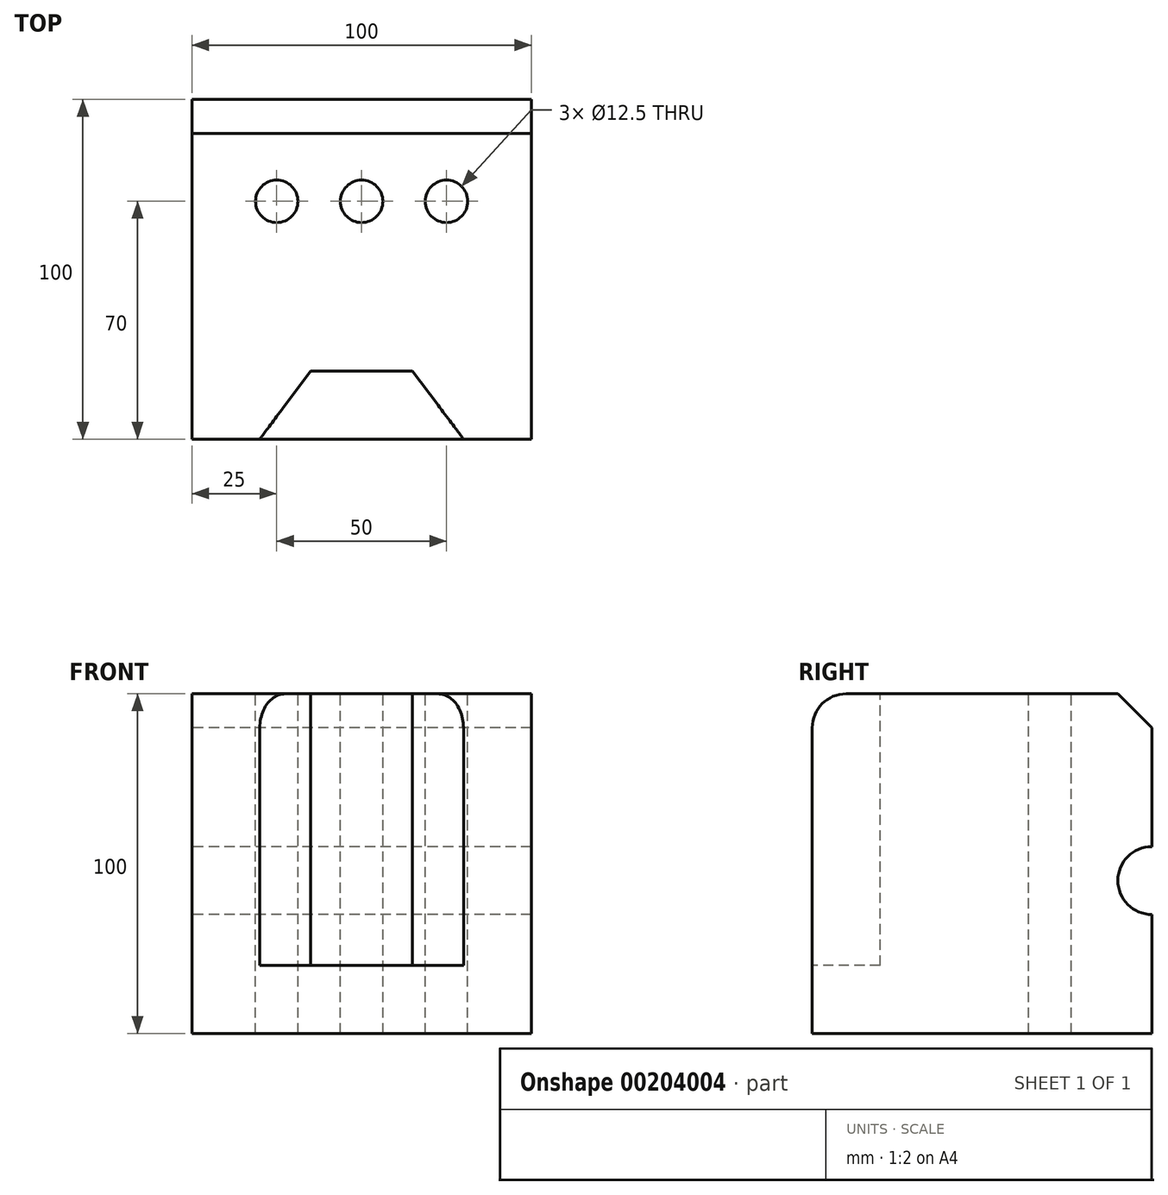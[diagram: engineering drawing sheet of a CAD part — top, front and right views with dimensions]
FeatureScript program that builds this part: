
annotation { "Feature Type Name" : "Feature", "Feature Type Description" : "" }
export const myFeature = defineFeature(function(context is Context, id is Id, definition is map)
    precondition{}
    {
        {
            var Q0;
            Q0=qCreatedBy(makeId("Front.planeOp"),FACE);
            var sketch = newSketch(context, id + "F0", { "sketchPlane" : qUnion([Q0])});
            skLineSegment(sketch, "E0.bottom", {"start": v(0, 0) * mm, "end": v(100, 0) * mm});
            skLineSegment(sketch, "E0.top", {"start": v(0, 100) * mm, "end": v(100, 100) * mm});
            skLineSegment(sketch, "E0.left", {"start": v(0, 0) * mm, "end": v(0, 100) * mm});
            skLineSegment(sketch, "E0.right", {"start": v(100, 0) * mm, "end": v(100, 100) * mm});
            skSolve(sketch);
        }
        {
            var Q0;
            Q0=makeQuery(id+"F0.imprint","IMPRINT",FACE,{"disambiguationData":[TD([[makeQuery(id+"F0.imprint","IMPRINT",EDGE,{"derivedFrom":sQuery(id+"F0.wireOp",EDGE,"E0.bottom")}),1.0]])]});
            extrude(context, id + "F1", {"entities" : qUnion([Q0]), "depth" : 100 * mm});
        }
        {
            var Q0;
            Q0=makeQuery(id+"F1.opExtrude","SWEPT_FACE",FACE,{"disambiguationData":[OSD([sQuery(id+"F0.wireOp",EDGE,"E0.top")])]});
            var sketch = newSketch(context, id + "F2", { "sketchPlane" : qUnion([Q0])});
            skCircle(sketch, "E1", {"center": v(25, -30) * mm, "radius": 6.25 * mm});
            skCircle(sketch, "E2", {"center": v(50, -30) * mm, "radius": 6.25 * mm});
            skCircle(sketch, "E3", {"center": v(75, -30) * mm, "radius": 6.25 * mm});
            skSolve(sketch);
        }
        {
            var Q0;
            Q0=makeQuery(id+"F2.imprint","IMPRINT",FACE,{"disambiguationData":[TD([[makeQuery(id+"F2.imprint","IMPRINT",EDGE,{"derivedFrom":sQuery(id+"F2.wireOp",EDGE,"E1")}),1.0]])]});
            var Q1;
            Q1=makeQuery(id+"F2.imprint","IMPRINT",FACE,{"disambiguationData":[TD([[makeQuery(id+"F2.imprint","IMPRINT",EDGE,{"derivedFrom":sQuery(id+"F2.wireOp",EDGE,"E2")}),1.0]])]});
            var Q2;
            Q2=makeQuery(id+"F2.imprint","IMPRINT",FACE,{"disambiguationData":[TD([[makeQuery(id+"F2.imprint","IMPRINT",EDGE,{"derivedFrom":sQuery(id+"F2.wireOp",EDGE,"E3")}),1.0]])]});
            var Q3;
            Q3=sQuery(id+"F2.wireOp",EDGE,"E2");
            var Q4;
            Q4=sQuery(id+"F2.wireOp",EDGE,"E3");
            var Q5;
            Q5=sQuery(id+"F2.wireOp",EDGE,"E1");
            extrude(context, id + "F3", {"entities" : qUnion([Q0, Q1, Q2]), "operationType" : NewBodyOperationType.REMOVE, "surfaceEntities" : qUnion([Q3, Q4, Q5]), "endBound" : BoundingType.THROUGH_ALL, "oppositeDirection" : true, "depth" : 25 * mm});
        }
        {
            var Q0;
            Q0=makeQuery(id+"F1.opExtrude","SWEPT_FACE",FACE,{"disambiguationData":[OSD([sQuery(id+"F0.wireOp",EDGE,"E0.top")])]});
            var sketch = newSketch(context, id + "F4", { "sketchPlane" : qUnion([Q0])});
            skLineSegment(sketch, "E4", {"start": v(35, -80) * mm, "end": v(65, -80) * mm});
            skLineSegment(sketch, "E5", {"start": v(65, -80) * mm, "end": v(80, -100) * mm});
            skLineSegment(sketch, "E6", {"start": v(80, -100) * mm, "end": v(20, -100) * mm});
            skLineSegment(sketch, "E7", {"start": v(20, -100) * mm, "end": v(35, -80) * mm});
            skSolve(sketch);
        }
        {
            var Q0;
            Q0=makeQuery(id+"F4.imprint","IMPRINT",FACE,{"disambiguationData":[TD([[makeQuery(id+"F4.imprint","IMPRINT",EDGE,{"derivedFrom":sQuery(id+"F4.wireOp",EDGE,"E4")}),-1.0]])]});
            extrude(context, id + "F5", {"entities" : qUnion([Q0]), "operationType" : NewBodyOperationType.REMOVE, "oppositeDirection" : true, "depth" : 80 * mm});
        }
        {
            var Q0;
            Q0=makeQuery(id+"F1.opExtrude","SWEPT_FACE",FACE,{"disambiguationData":[OSD([sQuery(id+"F0.wireOp",EDGE,"E0.left")])]});
            var sketch = newSketch(context, id + "F6", { "sketchPlane" : qUnion([Q0])});
            skCircle(sketch, "E8", {"center": v(0, 45) * mm, "radius": 10 * mm});
            skSolve(sketch);
        }
        {
            var Q0;
            {var subQ0=sQuery(id+"F6.wireOp",EDGE,"E8");var subQ1=makeQuery(id+"F1.opExtrude","CAP_EDGE",EDGE,{"disambiguationData":[OSD([sQuery(id+"F0.wireOp",EDGE,"E0.left")])],"isStart":true});var subQ2=makeQuery(id+"F6.imprint","INTERSECT",VERTEX,{"disambiguationData":[OD(0.0)],"derivedFrom":[subQ1,subQ0]});Q0=makeQuery(id+"F6.imprint","IMPRINT",FACE,{"disambiguationData":[TD([[makeQuery(id+"F6.imprint","IMPRINT",EDGE,{"disambiguationData":[TD([[subQ2,-1.0]])],"derivedFrom":subQ0}),1.0]])]});}
            var Q1;
            Q1=sQuery(id+"F6.wireOp",EDGE,"E8");
            extrude(context, id + "F7", {"entities" : qUnion([Q0]), "operationType" : NewBodyOperationType.REMOVE, "surfaceEntities" : qUnion([Q1]), "endBound" : BoundingType.THROUGH_ALL, "oppositeDirection" : true, "depth" : 25 * mm});
        }
        {
            var Q0;
            Q0=makeQuery(id+"F1.opExtrude","SWEPT_FACE",FACE,{"disambiguationData":[OSD([sQuery(id+"F0.wireOp",EDGE,"E0.left")])]});
            var sketch = newSketch(context, id + "F8", { "sketchPlane" : qUnion([Q0])});
            skLineSegment(sketch, "E9", {"start": v(10, 100) * mm, "end": v(0, 90) * mm});
            skLineSegment(sketch, "E10", {"start": v(0, 90) * mm, "end": v(0, 100) * mm});
            skLineSegment(sketch, "E11", {"start": v(0, 100) * mm, "end": v(10, 100) * mm});
            skSolve(sketch);
        }
        {
            var Q0;
            Q0=makeQuery(id+"F8.imprint","IMPRINT",FACE,{"disambiguationData":[TD([[makeQuery(id+"F8.imprint","IMPRINT",EDGE,{"derivedFrom":sQuery(id+"F8.wireOp",EDGE,"E9")}),-1.0]])]});
            extrude(context, id + "F9", {"entities" : qUnion([Q0]), "operationType" : NewBodyOperationType.REMOVE, "endBound" : BoundingType.THROUGH_ALL, "oppositeDirection" : true, "depth" : 25 * mm});
        }
        {
            var Q0;
            {var subQ0=sQuery(id+"F0.wireOp",EDGE,"E0.left");var subQ1=sQuery(id+"F0.wireOp",EDGE,"E0.top");Q0=makeQuery(id+"F5.boolean.opBoolean","SPLIT",EDGE,{"disambiguationData":[TD([makeQuery(id+"F1.opExtrude","SWEPT_FACE",FACE,{"disambiguationData":[OSD([subQ0])]})])],"derivedFrom":makeQuery(id+"F1.opExtrude","CAP_EDGE",EDGE,{"disambiguationData":[OSD([subQ1])],"isStart":false})});}
            var Q1;
            {var subQ0=sQuery(id+"F0.wireOp",EDGE,"E0.right");var subQ1=sQuery(id+"F0.wireOp",EDGE,"E0.top");Q1=makeQuery(id+"F5.boolean.opBoolean","SPLIT",EDGE,{"disambiguationData":[TD([makeQuery(id+"F1.opExtrude","SWEPT_FACE",FACE,{"disambiguationData":[OSD([subQ0])]})])],"derivedFrom":makeQuery(id+"F1.opExtrude","CAP_EDGE",EDGE,{"disambiguationData":[OSD([subQ1])],"isStart":false})});}
            fillet(context, id + "F10", {"entities" : qUnion([Q0, Q1]), "radius" : 10 * mm, "tangentPropagation" : true, "allowEdgeOverflow" : false});
        }
    });
